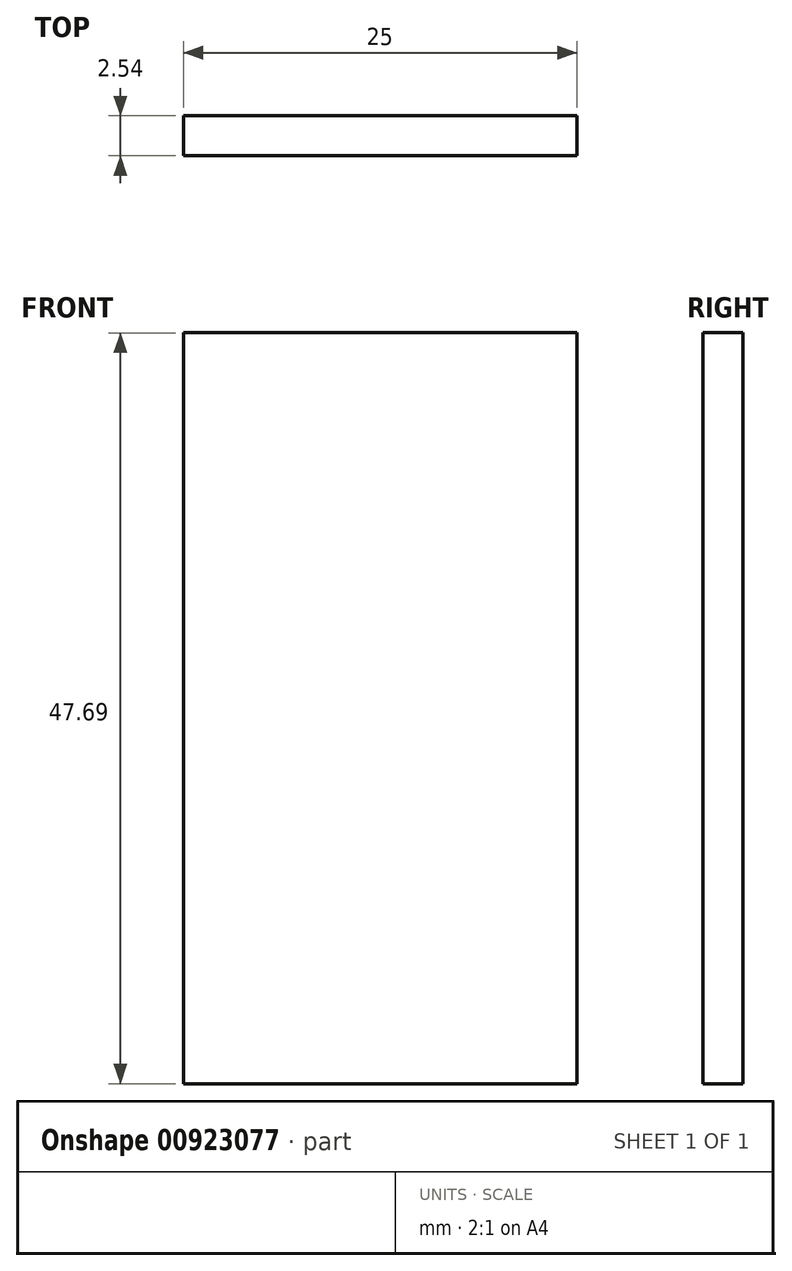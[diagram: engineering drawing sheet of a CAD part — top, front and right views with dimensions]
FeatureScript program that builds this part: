
annotation { "Feature Type Name" : "Feature", "Feature Type Description" : "" }
export const myFeature = defineFeature(function(context is Context, id is Id, definition is map)
    precondition{}
    {
        {
            var Q0;
            Q0=qCreatedBy(makeId("Right.planeOp"),FACE);
            var sketch = newSketch(context, id + "F0", { "sketchPlane" : qUnion([Q0])});
            skLineSegment(sketch, "E0", {"start": v(47.49, 50) * mm, "end": v(19.75, 50) * mm});
            skLineSegment(sketch, "E1.bottom", {"start": v(-17.73, 47.7) * mm, "end": v(-20.27, 47.7) * mm});
            skLineSegment(sketch, "E1.top", {"start": v(-17.73, 0) * mm, "end": v(-20.27, 0) * mm});
            skLineSegment(sketch, "E1.left", {"start": v(-17.73, 47.7) * mm, "end": v(-17.73, 0) * mm});
            skLineSegment(sketch, "E1.right", {"start": v(-20.27, 47.7) * mm, "end": v(-20.27, 0) * mm});
            skSolve(sketch);
        }
        {
            var Q0;
            Q0=makeQuery(id+"F0.imprint","IMPRINT",FACE,{"disambiguationData":[TD([[makeQuery(id+"F0.imprint","IMPRINT",EDGE,{"derivedFrom":sQuery(id+"F0.wireOp",EDGE,"E1.bottom")}),1.0]])]});
            var Q1;
            Q1=sQuery(id+"F0.wireOp",EDGE,"E1.right");
            var Q2;
            Q2=sQuery(id+"F0.wireOp",EDGE,"E1.left");
            var Q3;
            Q3=sQuery(id+"F0.wireOp",EDGE,"E1.bottom");
            var Q4;
            Q4=sQuery(id+"F0.wireOp",EDGE,"E1.top");
            extrude(context, id + "F1", {"entities" : qUnion([Q0]), "surfaceEntities" : qUnion([Q1, Q2, Q3, Q4]), "depth" : 25 * mm, "offsetDistance" : 25 * mm});
        }
    });
